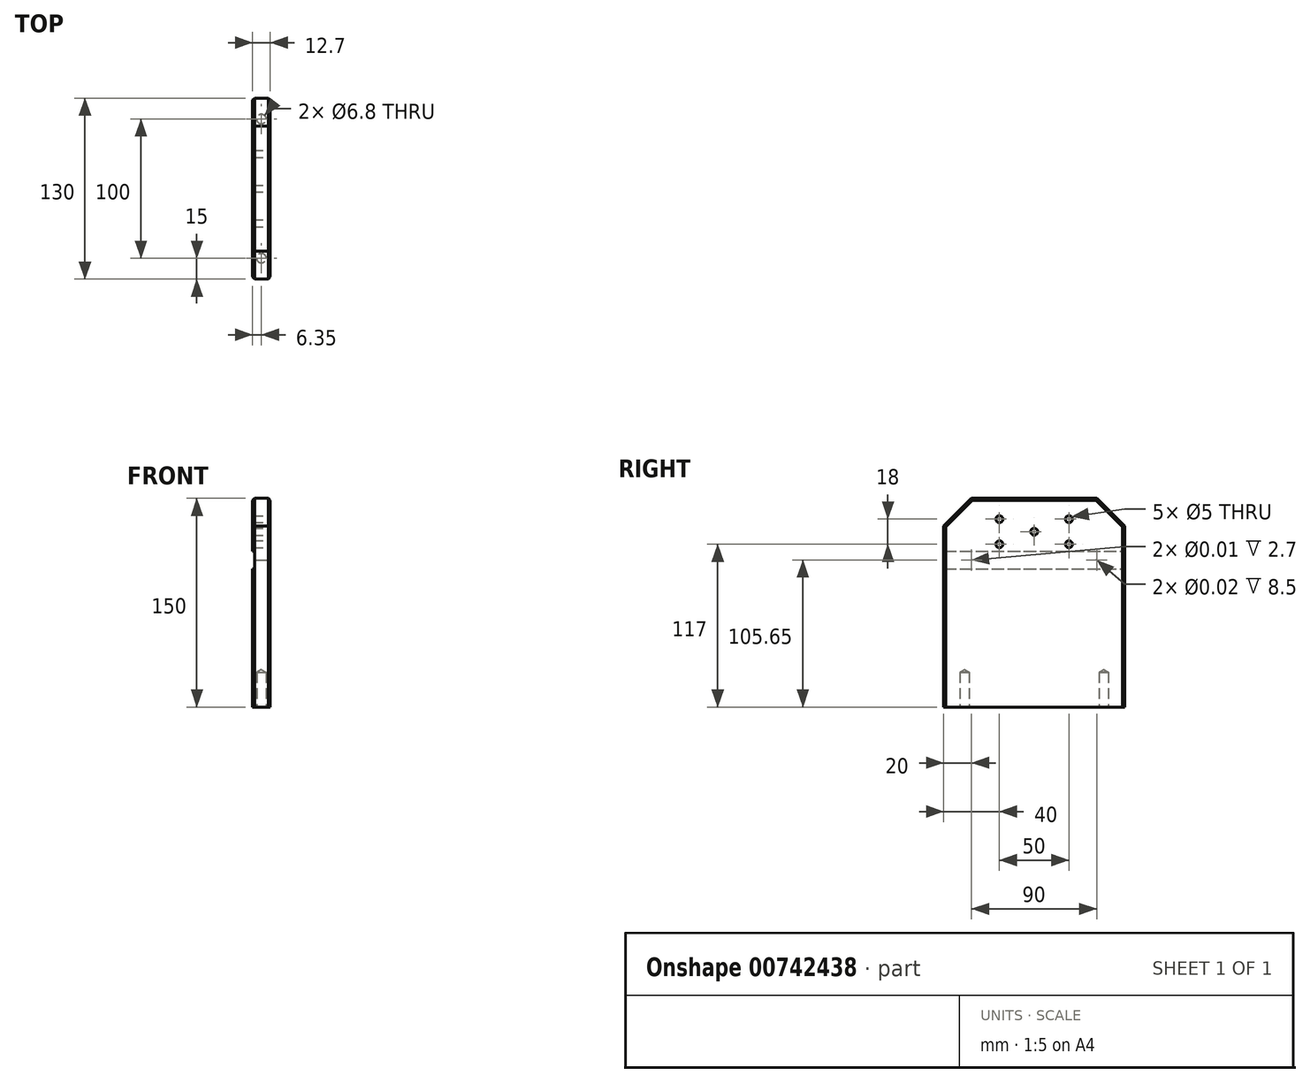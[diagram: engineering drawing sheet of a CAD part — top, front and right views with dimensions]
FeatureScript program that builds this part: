
annotation { "Feature Type Name" : "Feature", "Feature Type Description" : "" }
export const myFeature = defineFeature(function(context is Context, id is Id, definition is map)
    precondition{}
    {
        {
            var Q0;
            Q0=qCreatedBy(makeId("Right.planeOp"),FACE);
            var sketch = newSketch(context, id + "F0", { "sketchPlane" : qUnion([Q0])});
            skLineSegment(sketch, "E0.bottom", {"start": v(65, -75) * mm, "end": v(-65, -75) * mm});
            skLineSegment(sketch, "E0.top", {"start": v(65, 75) * mm, "end": v(-65, 75) * mm});
            skLineSegment(sketch, "E0.left", {"start": v(65, -75) * mm, "end": v(65, 75) * mm});
            skLineSegment(sketch, "E0.right", {"start": v(-65, -75) * mm, "end": v(-65, 75) * mm});
            skPoint(sketch, "E0.middle", {"position": v(0, 0) * mm});
            skSolve(sketch);
        }
        {
            var Q0;
            Q0=makeQuery(id+"F0.imprint","IMPRINT",FACE,{"disambiguationData":[TD([[makeQuery(id+"F0.imprint","IMPRINT",EDGE,{"derivedFrom":sQuery(id+"F0.wireOp",EDGE,"E0.bottom")}),-1.0]])]});
            extrude(context, id + "F1", {"entities" : qUnion([Q0]), "depth" : 12.7 * mm, "offsetDistance" : 25 * mm});
        }
        {
            var Q0;
            Q0=makeQuery(id+"F1.opExtrude","SWEPT_EDGE",EDGE,{"disambiguationData":[OSD([sQuery(id+"F0.wireOp",EDGE,"E0.top"),sQuery(id+"F0.wireOp",EDGE,"E0.right")])]});
            var Q1;
            Q1=makeQuery(id+"F1.opExtrude","SWEPT_EDGE",EDGE,{"disambiguationData":[OSD([sQuery(id+"F0.wireOp",EDGE,"E0.top"),sQuery(id+"F0.wireOp",EDGE,"E0.left")])]});
            chamfer(context, id + "F2", {"entities" : qUnion([Q0, Q1]), "width" : 20 * mm, "tangentPropagation" : true});
        }
        {
            var Q0;
            Q0=makeQuery(id+"F1.opExtrude","CAP_FACE",FACE,{"disambiguationData":[OSD([sQuery(id+"F0.wireOp",EDGE,"E0.bottom"),sQuery(id+"F0.wireOp",EDGE,"E0.top"),sQuery(id+"F0.wireOp",EDGE,"E0.left"),sQuery(id+"F0.wireOp",EDGE,"E0.right")])],"isStart":false});
            var sketch = newSketch(context, id + "F3", { "sketchPlane" : qUnion([Q0])});
            skPoint(sketch, "E1", {"position": v(45, 30.65) * mm});
            skPoint(sketch, "E2", {"position": v(-45, 30.65) * mm});
            skSolve(sketch);
        }
        {
            var Q0;
            Q0=sQuery(id+"F3.wireOp",VERTEX,"E1");
            var Q1;
            Q1=sQuery(id+"F3.wireOp",VERTEX,"E2");
            var Q2;
            Q2=makeQuery(id+"F1.opExtrude","SWEPT_BODY",BODY,{"disambiguationData":[OSD([sQuery(id+"F0.wireOp",EDGE,"E0.bottom"),sQuery(id+"F0.wireOp",EDGE,"E0.top"),sQuery(id+"F0.wireOp",EDGE,"E0.left"),sQuery(id+"F0.wireOp",EDGE,"E0.right")])]});
            hole(context, id + "F4", {"style" : HoleStyle.C_BORE, "endStyle" : HoleEndStyle.THROUGH, "standardTappedOrClearance" : lookupTablePath({ "standard" : "ANSI", "size" : "3/8 (0.38)", "type" : "Drilled" }), "standardBlindInLast" : lookupTablePath({ "standard" : "ANSI", "size" : "3/8", "type" : "Drilled" }), "holeDiameter" : 3 / 203.2 * mm, "cBoreDiameter" : 1 / 50.8 * mm, "cBoreDepth" : 8.5 * mm, "majorDiameter" : 6 * mm, "isTappedThrough" : true, "tappedDepth" : 20 * mm, "tapClearance" : 0, "startFromSketch" : true, "locations" : qUnion([Q0, Q1]), "scope" : qUnion([Q2])});
        }
        {
            var Q0;
            Q0=makeQuery(id+"F1.opExtrude","CAP_FACE",FACE,{"disambiguationData":[OSD([sQuery(id+"F0.wireOp",EDGE,"E0.bottom"),sQuery(id+"F0.wireOp",EDGE,"E0.top"),sQuery(id+"F0.wireOp",EDGE,"E0.left"),sQuery(id+"F0.wireOp",EDGE,"E0.right")])],"isStart":false});
            var sketch = newSketch(context, id + "F5", { "sketchPlane" : qUnion([Q0])});
            skPoint(sketch, "E3", {"position": v(25, 60) * mm});
            skPoint(sketch, "E4.0.1.0", {"position": v(25, 42) * mm});
            skPoint(sketch, "E4.1.0.0", {"position": v(-25, 60) * mm});
            skPoint(sketch, "E4.1.1.0", {"position": v(-25, 42) * mm});
            skLineSegment(sketch, "E4.direction1", {"start": v(25, 60) * mm, "end": v(-25, 60) * mm, "construction": true});
            skLineSegment(sketch, "E4.direction2", {"start": v(25, 60) * mm, "end": v(25, 42) * mm, "construction": true});
            skLineSegment(sketch, "E5", {"start": v(25, 60) * mm, "end": v(-25, 42) * mm});
            skPoint(sketch, "E6", {"position": v(0, 51) * mm});
            skSolve(sketch);
        }
        {
            var Q0;
            Q0=sQuery(id+"F5.wireOp",VERTEX,"E4.1.0.0");
            var Q1;
            Q1=sQuery(id+"F5.wireOp",VERTEX,"E3");
            var Q2;
            Q2=sQuery(id+"F5.wireOp",VERTEX,"E4.0.1.0");
            var Q3;
            Q3=sQuery(id+"F5.wireOp",VERTEX,"E6");
            var Q4;
            Q4=sQuery(id+"F5.wireOp",VERTEX,"E4.1.1.0");
            var Q5;
            Q5=makeQuery(id+"F1.opExtrude","SWEPT_BODY",BODY,{"disambiguationData":[OSD([sQuery(id+"F0.wireOp",EDGE,"E0.bottom"),sQuery(id+"F0.wireOp",EDGE,"E0.top"),sQuery(id+"F0.wireOp",EDGE,"E0.left"),sQuery(id+"F0.wireOp",EDGE,"E0.right")])]});
            hole(context, id + "F6", {"style" : HoleStyle.SIMPLE, "endStyle" : HoleEndStyle.THROUGH, "standardTappedOrClearance" : lookupTablePath({ "standard" : "ISO", "engagement" : "75%", "pitch" : "1 mm", "size" : "M6", "type" : "Tapped" }), "standardBlindInLast" : lookupTablePath({ "standard" : "ISO", "engagement" : "75%", "pitch" : "1 mm", "size" : "M6", "type" : "Tapped" }), "holeDiameter" : 5 * mm, "majorDiameter" : 6 * mm, "showTappedDepth" : true, "isTappedThrough" : true, "tappedDepth" : 20 * mm, "tapClearance" : 0, "startFromSketch" : true, "locations" : qUnion([Q0, Q1, Q2, Q3, Q4]), "scope" : qUnion([Q5])});
        }
        {
            var Q0;
            Q0=makeQuery(id+"F1.opExtrude","CAP_FACE",FACE,{"disambiguationData":[OSD([sQuery(id+"F0.wireOp",EDGE,"E0.bottom"),sQuery(id+"F0.wireOp",EDGE,"E0.top"),sQuery(id+"F0.wireOp",EDGE,"E0.left"),sQuery(id+"F0.wireOp",EDGE,"E0.right")])],"isStart":true});
            var sketch = newSketch(context, id + "F7", { "sketchPlane" : qUnion([Q0])});
            skCircle(sketch, "E7.0", {"center": v(-45, 30.65) * mm, "radius": 4.76 * mm});
            skCircle(sketch, "E8.0", {"center": v(45, 30.65) * mm, "radius": 4.76 * mm});
            skLineSegment(sketch, "E9", {"start": v(-45, 30.65) * mm, "end": v(45, 30.65) * mm, "construction": true});
            skLineSegment(sketch, "E10.bottom", {"start": v(65, 24.25) * mm, "end": v(-65, 24.25) * mm});
            skLineSegment(sketch, "E10.top", {"start": v(65, 37.05) * mm, "end": v(-65, 37.05) * mm});
            skLineSegment(sketch, "E10.left", {"start": v(65, 24.25) * mm, "end": v(65, 37.05) * mm});
            skLineSegment(sketch, "E10.right", {"start": v(-65, 24.25) * mm, "end": v(-65, 37.05) * mm});
            skPoint(sketch, "E10.middle", {"position": v(0, 30.65) * mm});
            skSolve(sketch);
        }
        {
            var Q0;
            Q0=makeQuery(id+"F7.imprint","IMPRINT",FACE,{"disambiguationData":[TD([[makeQuery(id+"F7.imprint","IMPRINT",EDGE,{"derivedFrom":sQuery(id+"F7.wireOp",EDGE,"E7.0")}),-1.0]])]});
            var Q1;
            Q1=makeQuery(id+"F7.imprint","IMPRINT",FACE,{"disambiguationData":[TD([[makeQuery(id+"F7.imprint","IMPRINT",EDGE,{"derivedFrom":sQuery(id+"F7.wireOp",EDGE,"E7.0")}),1.0]])]});
            var Q2;
            Q2=makeQuery(id+"F7.imprint","IMPRINT",FACE,{"disambiguationData":[TD([[makeQuery(id+"F7.imprint","IMPRINT",EDGE,{"derivedFrom":sQuery(id+"F7.wireOp",EDGE,"E8.0")}),1.0]])]});
            extrude(context, id + "F8", {"entities" : qUnion([Q0, Q1, Q2]), "operationType" : NewBodyOperationType.REMOVE, "oppositeDirection" : true, "depth" : 1.5 * mm, "offsetDistance" : 25 * mm});
        }
        {
            var Q0;
            Q0=makeQuery(id+"F1.opExtrude","SWEPT_FACE",FACE,{"disambiguationData":[OSD([sQuery(id+"F0.wireOp",EDGE,"E0.bottom")])]});
            var sketch = newSketch(context, id + "F9", { "sketchPlane" : qUnion([Q0])});
            skPoint(sketch, "E11", {"position": v(6.35, 50) * mm});
            skPoint(sketch, "E11.positionSnap0", {"position": v(6.35, 65) * mm});
            skPoint(sketch, "E12", {"position": v(6.35, -50) * mm});
            skSolve(sketch);
        }
        {
            var Q0;
            Q0=sQuery(id+"F9.wireOp",VERTEX,"E11");
            var Q1;
            Q1=sQuery(id+"F9.wireOp",VERTEX,"E12");
            var Q2;
            Q2=makeQuery(id+"F1.opExtrude","SWEPT_BODY",BODY,{"disambiguationData":[OSD([sQuery(id+"F0.wireOp",EDGE,"E0.bottom"),sQuery(id+"F0.wireOp",EDGE,"E0.top"),sQuery(id+"F0.wireOp",EDGE,"E0.left"),sQuery(id+"F0.wireOp",EDGE,"E0.right")])]});
            hole(context, id + "F10", {"style" : HoleStyle.SIMPLE, "endStyle" : HoleEndStyle.BLIND, "standardTappedOrClearance" : lookupTablePath({ "standard" : "ISO", "engagement" : "75%", "pitch" : "1.25 mm", "size" : "M8", "type" : "Tapped" }), "standardBlindInLast" : lookupTablePath({ "standard" : "ISO", "engagement" : "75%", "pitch" : "1.25 mm", "size" : "M8", "type" : "Tapped" }), "holeDiameter" : 6.8 * mm, "majorDiameter" : 8 * mm, "showTappedDepth" : true, "holeDepth" : 25 * mm, "isTappedThrough" : true, "tappedDepth" : 25 * mm, "tapClearance" : 0, "startFromSketch" : true, "locations" : qUnion([Q0, Q1]), "scope" : qUnion([Q2])});
        }
        {
            var Q0;
            {var subQ0=sQuery(id+"F0.wireOp",EDGE,"E0.bottom");var subQ1=sQuery(id+"F0.wireOp",EDGE,"E0.right");Q0=makeQuery(id+"F8.boolean.opBoolean","SPLIT",EDGE,{"disambiguationData":[TD([makeQuery(id+"F1.opExtrude","SWEPT_FACE",FACE,{"disambiguationData":[OSD([subQ0])]})])],"derivedFrom":makeQuery(id+"F1.opExtrude","CAP_EDGE",EDGE,{"disambiguationData":[OSD([subQ1])],"isStart":true})});}
            var Q1;
            {var subQ0=sQuery(id+"F0.wireOp",EDGE,"E0.right");Q1=makeQuery(id+"F8.boolean.opBoolean","SPLIT",EDGE,{"disambiguationData":[TD([makeQuery(id+"F8.opExtrude","SWEPT_FACE",FACE,{"disambiguationData":[OSD([sQuery(id+"F7.wireOp",EDGE,"E10.top")])]})])],"derivedFrom":makeQuery(id+"F1.opExtrude","CAP_EDGE",EDGE,{"disambiguationData":[OSD([subQ0])],"isStart":true})});}
            var Q2;
            {var subQ0=sQuery(id+"F0.wireOp",EDGE,"E0.right");var subQ1=sQuery(id+"F0.wireOp",EDGE,"E0.top");Q2=makeQuery(id+"F2.opChamfer","BLEND_EDGE",EDGE,{"blendedFrom":[makeQuery(id+"F1.opExtrude","SWEPT_EDGE",EDGE,{"disambiguationData":[OSD([subQ1,subQ0])]}),makeQuery(id+"F1.opExtrude","CAP_FACE",FACE,{"disambiguationData":[OSD([sQuery(id+"F0.wireOp",EDGE,"E0.bottom"),subQ1,sQuery(id+"F0.wireOp",EDGE,"E0.left"),subQ0])],"isStart":true})],"blendedInto":[makeQuery(id+"F1.opExtrude","CAP_FACE",FACE,{"disambiguationData":[OSD([sQuery(id+"F0.wireOp",EDGE,"E0.bottom"),subQ1,sQuery(id+"F0.wireOp",EDGE,"E0.left"),subQ0])],"isStart":true})]});}
            var Q3;
            Q3=makeQuery(id+"F1.opExtrude","CAP_EDGE",EDGE,{"disambiguationData":[OSD([sQuery(id+"F0.wireOp",EDGE,"E0.top")])],"isStart":true});
            var Q4;
            {var subQ0=sQuery(id+"F0.wireOp",EDGE,"E0.left");var subQ1=sQuery(id+"F0.wireOp",EDGE,"E0.top");Q4=makeQuery(id+"F2.opChamfer","BLEND_EDGE",EDGE,{"blendedFrom":[makeQuery(id+"F1.opExtrude","SWEPT_EDGE",EDGE,{"disambiguationData":[OSD([subQ1,subQ0])]}),makeQuery(id+"F1.opExtrude","CAP_FACE",FACE,{"disambiguationData":[OSD([sQuery(id+"F0.wireOp",EDGE,"E0.bottom"),subQ1,subQ0,sQuery(id+"F0.wireOp",EDGE,"E0.right")])],"isStart":true})],"blendedInto":[makeQuery(id+"F1.opExtrude","CAP_FACE",FACE,{"disambiguationData":[OSD([sQuery(id+"F0.wireOp",EDGE,"E0.bottom"),subQ1,subQ0,sQuery(id+"F0.wireOp",EDGE,"E0.right")])],"isStart":true})]});}
            var Q5;
            {var subQ0=sQuery(id+"F0.wireOp",EDGE,"E0.left");Q5=makeQuery(id+"F8.boolean.opBoolean","SPLIT",EDGE,{"disambiguationData":[TD([makeQuery(id+"F8.opExtrude","SWEPT_FACE",FACE,{"disambiguationData":[OSD([sQuery(id+"F7.wireOp",EDGE,"E10.top")])]})])],"derivedFrom":makeQuery(id+"F1.opExtrude","CAP_EDGE",EDGE,{"disambiguationData":[OSD([subQ0])],"isStart":true})});}
            var Q6;
            {var subQ0=sQuery(id+"F0.wireOp",EDGE,"E0.bottom");var subQ1=sQuery(id+"F0.wireOp",EDGE,"E0.left");Q6=makeQuery(id+"F8.boolean.opBoolean","SPLIT",EDGE,{"disambiguationData":[TD([makeQuery(id+"F1.opExtrude","SWEPT_FACE",FACE,{"disambiguationData":[OSD([subQ0])]})])],"derivedFrom":makeQuery(id+"F1.opExtrude","CAP_EDGE",EDGE,{"disambiguationData":[OSD([subQ1])],"isStart":true})});}
            var Q7;
            Q7=makeQuery(id+"F1.opExtrude","CAP_EDGE",EDGE,{"disambiguationData":[OSD([sQuery(id+"F0.wireOp",EDGE,"E0.left")])],"isStart":false});
            var Q8;
            {var subQ0=sQuery(id+"F0.wireOp",EDGE,"E0.left");var subQ1=sQuery(id+"F0.wireOp",EDGE,"E0.top");Q8=makeQuery(id+"F2.opChamfer","BLEND_EDGE",EDGE,{"blendedFrom":[makeQuery(id+"F1.opExtrude","SWEPT_EDGE",EDGE,{"disambiguationData":[OSD([subQ1,subQ0])]}),makeQuery(id+"F1.opExtrude","CAP_FACE",FACE,{"disambiguationData":[OSD([sQuery(id+"F0.wireOp",EDGE,"E0.bottom"),subQ1,subQ0,sQuery(id+"F0.wireOp",EDGE,"E0.right")])],"isStart":false})],"blendedInto":[makeQuery(id+"F1.opExtrude","CAP_FACE",FACE,{"disambiguationData":[OSD([sQuery(id+"F0.wireOp",EDGE,"E0.bottom"),subQ1,subQ0,sQuery(id+"F0.wireOp",EDGE,"E0.right")])],"isStart":false})]});}
            var Q9;
            Q9=makeQuery(id+"F1.opExtrude","CAP_EDGE",EDGE,{"disambiguationData":[OSD([sQuery(id+"F0.wireOp",EDGE,"E0.top")])],"isStart":false});
            var Q10;
            {var subQ0=sQuery(id+"F0.wireOp",EDGE,"E0.right");var subQ1=sQuery(id+"F0.wireOp",EDGE,"E0.top");Q10=makeQuery(id+"F2.opChamfer","BLEND_EDGE",EDGE,{"blendedFrom":[makeQuery(id+"F1.opExtrude","SWEPT_EDGE",EDGE,{"disambiguationData":[OSD([subQ1,subQ0])]}),makeQuery(id+"F1.opExtrude","CAP_FACE",FACE,{"disambiguationData":[OSD([sQuery(id+"F0.wireOp",EDGE,"E0.bottom"),subQ1,sQuery(id+"F0.wireOp",EDGE,"E0.left"),subQ0])],"isStart":false})],"blendedInto":[makeQuery(id+"F1.opExtrude","CAP_FACE",FACE,{"disambiguationData":[OSD([sQuery(id+"F0.wireOp",EDGE,"E0.bottom"),subQ1,sQuery(id+"F0.wireOp",EDGE,"E0.left"),subQ0])],"isStart":false})]});}
            var Q11;
            Q11=makeQuery(id+"F1.opExtrude","CAP_EDGE",EDGE,{"disambiguationData":[OSD([sQuery(id+"F0.wireOp",EDGE,"E0.right")])],"isStart":false});
            chamfer(context, id + "F11", {"entities" : qUnion([Q0, Q1, Q2, Q3, Q4, Q5, Q6, Q7, Q8, Q9, Q10, Q11]), "width" : 1.5 * mm, "tangentPropagation" : true});
        }
    });
